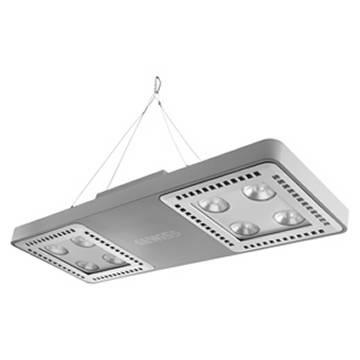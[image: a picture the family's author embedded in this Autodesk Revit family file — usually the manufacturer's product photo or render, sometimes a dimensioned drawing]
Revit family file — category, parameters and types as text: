
# Revit family: Lighting-Industriale-GEWISS-SMART[4]HE_APPARECCHI-LED_2M
name_source: partatom
category: Apparecchi per illuminazione
units: mm (PartAtom-declared; Revit-internal decimal feet)

## family parameters
Basato su piano di lavoro = Sì
Condiviso = No
Numero OmniClass = 23.80.70.00
Punto di calcolo locali = No
Quota connettore circolare = Usa diametro
Sempre verticale = No
Sorgente d'illuminazione = No
Taglio con vuoti quando caricato = No
Tipo di parte = Normale
Titolo OmniClass = Lighting

## types (1)
- Lighting-Industriale-GEWISS-SMART[4]HE_APPARECCHI-LED_2M
    Alimentatore = Incluso
    Apparecchio a ridotta temperatura superficiale = Si
    Applicazione = Interno
    Cablaggio = Con connettore stagno Gw connect
    Caratteristiche elettriche e gestione della luce = -
    Caratteristiche ottiche e illuminotecniche = -
    Carico apparente = 97 VA
    Catalogo = LIGHTING
    Certificazione DIN 18032-3 = Con Staffa - Kit Funi + morsetto (in approvazione)
    Certificazioni e classificazioni = -
    Classe fotobiologica = RG0
    Classe isolamento = I
    Classificazione = Lighting
    Classificazione: = -
    Codice Electrocod = 2444
    Codice digitale univoco (Datamatrix) = Datamatrix
    Colore = Grigio RAL 7035
    Commenti sul wattaggio = 97W
    Contesto = Illuminazione di industrie e impianti sportivi
    Controllo abbagliamento e luminanza = -
    Corpo = PA6 “Halogen Free” caricato fibra vetro
    Descrizione = SMART[4]HB 2M C.PAS.ON/OFF ELL.57K
    Dispositivo di protezione = DM 6kV / CM 6kV
    Dist_sorg_lum = 10 mm  [stored 0.0328084 ft]
    Durata di vita = L90B10 (Tq+25°C) = 70.000 h - L90B10 (Tq+50°C) = 35.000 h
    Efficienza luminosa (lm/W) = 129
    Finitura colore = Grigio RAL 7035
    Fissaggio = -
    Frequenza nominale (Hz) = 50/60 Hz
    Gancio di chiusura = -
    Garanzia = 5 anni
    Grado di protezione = IP66
    Gruppo ottico = Riflettore in PC metallizzato e lenti in PMMA
    Guarnizioni = tipo siliconico antinvecchiamento
    IDF = fd6a7348-9c72-479e-b250-f075bd14036a
    IDT = 170d63836ef34e7a91627e9879a3eea4
    IPEA = -
    Immagine tipo = GWL1311.jpg
    Inclinazione = Con accessorio staffa
    Indice di resa cromatica = CRI-80
    Informazioni generali = -
    Installazione e manutenzione = -
    Lampada = LED
    Larghezza = 254 mm
    Lumen output (lm) = 12300
    Lunghezza = 699 mm  [stored 2.29331 ft]
    Mascherina = <Per categoria>
    Materiali = -
    Modello = GWS4222AQ857
    Motore = <Per categoria>
    Norma di riferimento = EN 60598-1 ; EN 60598-2-1 ; EN 60598-2-24
    Ottica = Ellittica
    Peso (kg): = 6,5
    Potenza di sistema = 95W
    Produttore = GEWISS S.p.A.
    Prospetto di default = 1219 mm
    Resistenza agli urti = IK08
    Resistenza al filo incandescente = 850 °C
    SEO = High bay
    Scheda Tecnica = https://www.gewiss.com
    Schermo = Vetro Temprato Spessore 4mm
    Sistema di controllo = ON / OFF
    Sistema di controllo : = ON / OFF
    Sostituibilità gruppo ottico = Non sostituibile
    Sostituibilità piastra di cablaggio = Non sostituibile
    Spessore plafoniera = 40 mm  [stored 0.131234 ft]
    Struttura plafoniera = <Per categoria>
    Superficie massima esposta al vento : = 0,184 m²
    Temperatura di colore = 5700K
    Temperatura di esercizio = -30°C ÷ +50 °C
    Temperatura di stoccaggio = -40 +70 °C
    Tensione di alimentazione = 220 - 240 V
    Tipo di apparecchio = Riflettore industriale a LED&nbsp;
    Tipo di installazione e montaggio = Plafone - Parete - Sospensione
    Tipologia sorgente luminosa = LED - Non sostituibile
    Tolleranza cromatica = SDCM = 3
    Trasformatore = <Per categoria>
    URL = https://www.gewiss.com
    Vano di alimentazione = Integrato
    Versione file RFA = 20.11
    Viti esterne = Acciaio inox
    Voltaggio = 230 V

note: [stored X ft] marks values corroborated as IEEE doubles in the binary element streams (Revit-internal decimal feet)

## geometry (parser evidence)
native form markers: Blend x4, Sweep x3
no freeform markers — native parametric forms only
